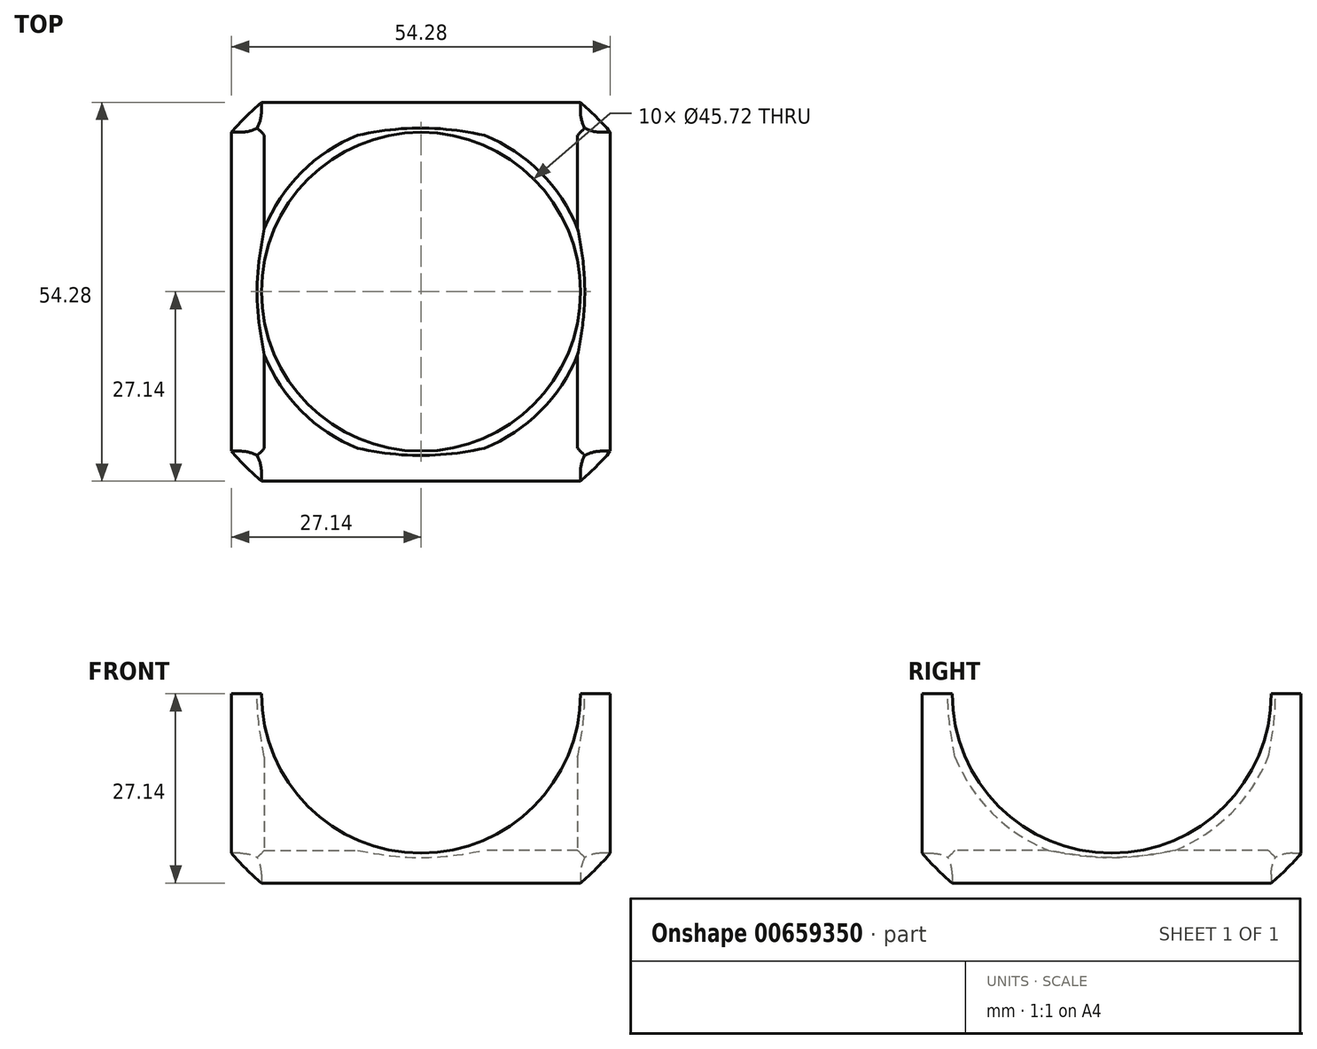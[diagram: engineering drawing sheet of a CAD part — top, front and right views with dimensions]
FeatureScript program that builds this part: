
annotation { "Feature Type Name" : "Feature", "Feature Type Description" : "" }
export const myFeature = defineFeature(function(context is Context, id is Id, definition is map)
    precondition{}
    {
        {
            var Q0;
            Q0=qCreatedBy(makeId("Top.planeOp"),FACE);
            var sketch = newSketch(context, id + "F0", { "sketchPlane" : qUnion([Q0])});
            skCircle(sketch, "E0", {"center": v(0, 0) * mm, "radius": 35.49 * mm});
            skLineSegment(sketch, "E1", {"start": v(0, -35.49) * mm, "end": v(0, 35.49) * mm});
            skSolve(sketch);
        }
        {
            var Q0;
            {var subQ0=sQuery(id+"F0.wireOp",EDGE,"E1");Q0=makeQuery(id+"F0.imprint","IMPRINT",FACE,{"disambiguationData":[TD([[makeQuery(id+"F0.imprint","IMPRINT",EDGE,{"derivedFrom":subQ0}),1.0]])]});}
            var Q1;
            Q1=sQuery(id+"F0.wireOp",EDGE,"E1");
            revolve(context, id + "F1", {"entities" : qUnion([Q0]), "axis" : qUnion([Q1]), "revolveType" : RevolveType.FULL});
        }
        {
            var Q0;
            Q0=qCreatedBy(makeId("Front.planeOp"),FACE);
            var sketch = newSketch(context, id + "F2", { "sketchPlane" : qUnion([Q0])});
            skCircle(sketch, "E2", {"center": v(0, 0) * mm, "radius": 22.86 * mm});
            skSolve(sketch);
        }
        {
            var Q0;
            Q0=qSketchRegion(id+"F2",true);
            extrude(context, id + "F3", {"entities" : qUnion([Q0]), "operationType" : NewBodyOperationType.REMOVE, "endBound" : BoundingType.SYMMETRIC, "depth" : 76.2 * mm, "offsetDistance" : 25.4 * mm});
        }
        {
            var Q0;
            Q0=qCreatedBy(makeId("Right.planeOp"),FACE);
            var sketch = newSketch(context, id + "F4", { "sketchPlane" : qUnion([Q0])});
            skCircle(sketch, "E3", {"center": v(0, 0) * mm, "radius": 22.86 * mm});
            skSolve(sketch);
        }
        {
            var Q0;
            Q0=makeQuery(id+"F4.imprint","IMPRINT",FACE,{"disambiguationData":[TD([[makeQuery(id+"F4.imprint","IMPRINT",EDGE,{"derivedFrom":sQuery(id+"F4.wireOp",EDGE,"E3")}),1.0]])]});
            extrude(context, id + "F5", {"entities" : qUnion([Q0]), "operationType" : NewBodyOperationType.REMOVE, "endBound" : BoundingType.SYMMETRIC, "depth" : 76.2 * mm, "offsetDistance" : 25.4 * mm});
        }
        {
            var Q0;
            Q0=qCreatedBy(makeId("Top.planeOp"),FACE);
            var sketch = newSketch(context, id + "F6", { "sketchPlane" : qUnion([Q0])});
            skCircle(sketch, "E4", {"center": v(0, 0) * mm, "radius": 22.86 * mm});
            skSolve(sketch);
        }
        {
            var Q0;
            Q0=qSketchRegion(id+"F6",true);
            extrude(context, id + "F7", {"entities" : qUnion([Q0]), "operationType" : NewBodyOperationType.REMOVE, "endBound" : BoundingType.SYMMETRIC, "depth" : 76.2 * mm, "offsetDistance" : 25.4 * mm});
        }
        {
            var Q0;
            Q0=qCreatedBy(makeId("Top.planeOp"),FACE);
            var sketch = newSketch(context, id + "F8", { "sketchPlane" : qUnion([Q0])});
            skCircle(sketch, "E5", {"center": v(0, 0) * mm, "radius": 33.02 * mm});
            skLineSegment(sketch, "E6", {"start": v(0, 33.02) * mm, "end": v(0, -33.02) * mm});
            skSolve(sketch);
        }
        {
            var Q0;
            {var subQ0=sQuery(id+"F8.wireOp",EDGE,"E6");Q0=makeQuery(id+"F8.imprint","IMPRINT",FACE,{"disambiguationData":[TD([[makeQuery(id+"F8.imprint","IMPRINT",EDGE,{"derivedFrom":subQ0}),-1.0]])]});}
            var Q1;
            Q1=sQuery(id+"F8.wireOp",EDGE,"E6");
            revolve(context, id + "F9", {"operationType" : NewBodyOperationType.REMOVE, "entities" : qUnion([Q0]), "axis" : qUnion([Q1]), "revolveType" : RevolveType.FULL});
        }
        {
            var Q0;
            Q0=makeQuery(id+"F9.boolean.opBoolean","INTERSECT",EDGE,{"derivedFrom":[makeQuery(id+"F5.boolean.opBoolean","COPY",FACE,{"disambiguationData":[OD(1.0)],"derivedFrom":makeQuery(id+"F5.opExtrude","SWEPT_FACE",FACE,{"disambiguationData":[OSD([sQuery(id+"F4.wireOp",EDGE,"E3")])]})}),makeQuery(id+"F9.opRevolve","SWEPT_FACE",FACE,{"disambiguationData":[OSD([sQuery(id+"F8.wireOp",EDGE,"E5")])]})]});
            var Q1;
            Q1=makeQuery(id+"F9.boolean.opBoolean","INTERSECT",EDGE,{"derivedFrom":[makeQuery(id+"F7.boolean.opBoolean","COPY",FACE,{"disambiguationData":[OD(0.0)],"derivedFrom":makeQuery(id+"F7.opExtrude","SWEPT_FACE",FACE,{"disambiguationData":[OSD([sQuery(id+"F6.wireOp",EDGE,"E4")])]})}),makeQuery(id+"F9.opRevolve","SWEPT_FACE",FACE,{"disambiguationData":[OSD([sQuery(id+"F8.wireOp",EDGE,"E5")])]})]});
            var Q2;
            Q2=makeQuery(id+"F9.boolean.opBoolean","INTERSECT",EDGE,{"derivedFrom":[makeQuery(id+"F5.boolean.opBoolean","SPLIT",FACE,{"disambiguationData":[OD(1.0)],"derivedFrom":makeQuery(id+"F3.boolean.opBoolean","COPY",FACE,{"derivedFrom":makeQuery(id+"F3.opExtrude","SWEPT_FACE",FACE,{"disambiguationData":[OSD([sQuery(id+"F2.wireOp",EDGE,"E2")])]})})}),makeQuery(id+"F9.opRevolve","SWEPT_FACE",FACE,{"disambiguationData":[OSD([sQuery(id+"F8.wireOp",EDGE,"E5")])]})]});
            var Q3;
            Q3=makeQuery(id+"F9.boolean.opBoolean","INTERSECT",EDGE,{"derivedFrom":[makeQuery(id+"F5.boolean.opBoolean","SPLIT",FACE,{"disambiguationData":[OD(0.0)],"derivedFrom":makeQuery(id+"F3.boolean.opBoolean","COPY",FACE,{"derivedFrom":makeQuery(id+"F3.opExtrude","SWEPT_FACE",FACE,{"disambiguationData":[OSD([sQuery(id+"F2.wireOp",EDGE,"E2")])]})})}),makeQuery(id+"F9.opRevolve","SWEPT_FACE",FACE,{"disambiguationData":[OSD([sQuery(id+"F8.wireOp",EDGE,"E5")])]})]});
            var Q4;
            Q4=makeQuery(id+"F9.boolean.opBoolean","INTERSECT",EDGE,{"derivedFrom":[makeQuery(id+"F5.boolean.opBoolean","COPY",FACE,{"disambiguationData":[OD(0.0)],"derivedFrom":makeQuery(id+"F5.opExtrude","SWEPT_FACE",FACE,{"disambiguationData":[OSD([sQuery(id+"F4.wireOp",EDGE,"E3")])]})}),makeQuery(id+"F9.opRevolve","SWEPT_FACE",FACE,{"disambiguationData":[OSD([sQuery(id+"F8.wireOp",EDGE,"E5")])]})]});
            var Q5;
            Q5=makeQuery(id+"F9.boolean.opBoolean","INTERSECT",EDGE,{"derivedFrom":[makeQuery(id+"F7.boolean.opBoolean","COPY",FACE,{"disambiguationData":[OD(1.0)],"derivedFrom":makeQuery(id+"F7.opExtrude","SWEPT_FACE",FACE,{"disambiguationData":[OSD([sQuery(id+"F6.wireOp",EDGE,"E4")])]})}),makeQuery(id+"F9.opRevolve","SWEPT_FACE",FACE,{"disambiguationData":[OSD([sQuery(id+"F8.wireOp",EDGE,"E5")])]})]});
            fillet(context, id + "F10", {"entities" : qUnion([Q0, Q1, Q2, Q3, Q4, Q5]), "radius" : 5.08 * mm, "tangentPropagation" : true, "allowEdgeOverflow" : false});
        }
        {
            var Q0;
            Q0=qCreatedBy(makeId("Front.planeOp"),FACE);
            var sketch = newSketch(context, id + "F11", { "sketchPlane" : qUnion([Q0])});
            skLineSegment(sketch, "E7.bottom", {"start": v(-37.9, 28.56) * mm, "end": v(45.42, 28.56) * mm});
            skLineSegment(sketch, "E7.top", {"start": v(-37.9, 0) * mm, "end": v(45.42, 0) * mm});
            skLineSegment(sketch, "E7.left", {"start": v(-37.9, 28.56) * mm, "end": v(-37.9, 0) * mm});
            skLineSegment(sketch, "E7.right", {"start": v(45.42, 28.56) * mm, "end": v(45.42, 0) * mm});
            skSolve(sketch);
        }
        {
            var Q0;
            Q0=makeQuery(id+"F11.imprint","IMPRINT",FACE,{"disambiguationData":[TD([[makeQuery(id+"F11.imprint","IMPRINT",EDGE,{"derivedFrom":sQuery(id+"F11.wireOp",EDGE,"E7.bottom")}),-1.0]])]});
            extrude(context, id + "F12", {"entities" : qUnion([Q0]), "operationType" : NewBodyOperationType.REMOVE, "endBound" : BoundingType.SYMMETRIC, "depth" : 76.2 * mm, "offsetDistance" : 25.4 * mm});
        }
    });
